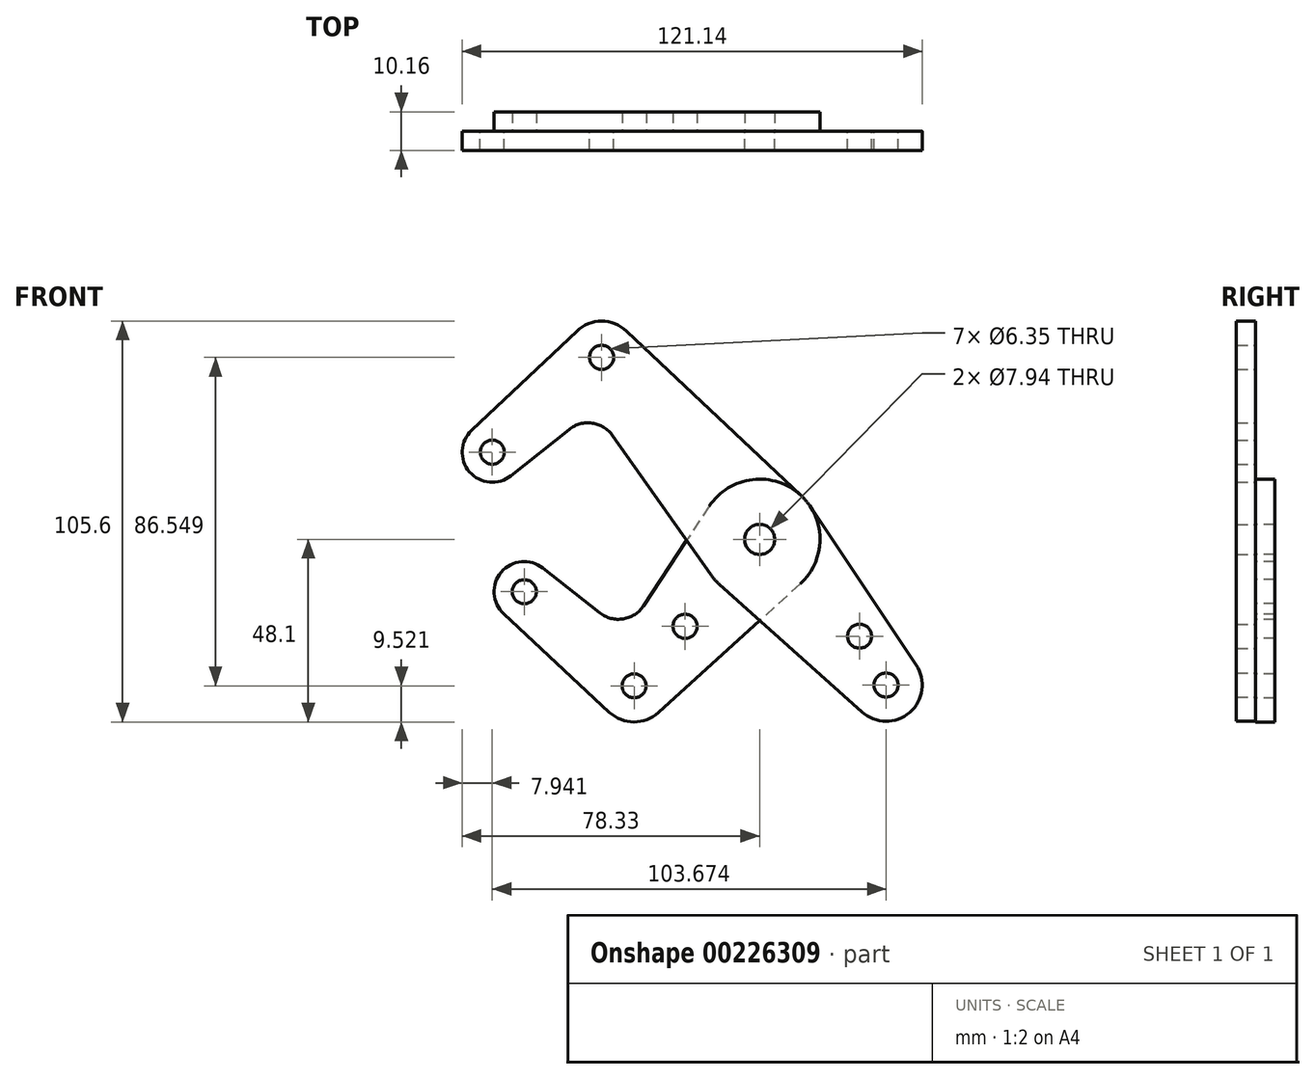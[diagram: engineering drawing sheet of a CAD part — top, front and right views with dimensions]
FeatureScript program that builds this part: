
annotation { "Feature Type Name" : "Feature", "Feature Type Description" : "" }
export const myFeature = defineFeature(function(context is Context, id is Id, definition is map)
    precondition{}
    {
        {
            var Q0;
            Q0=qCreatedBy(makeId("Front.planeOp"),FACE);
            var sketch = newSketch(context, id + "F0", { "sketchPlane" : qUnion([Q0])});
            skLineSegment(sketch, "E0", {"start": v(-41.6, 47.97) * mm, "end": v(41.6, -47.97) * mm, "construction": true});
            skCircle(sketch, "E1", {"center": v(0, 0) * mm, "radius": 3.18 * mm});
            skCircle(sketch, "E2", {"center": v(33.29, -38.38) * mm, "radius": 3.18 * mm});
            skCircle(sketch, "E3", {"center": v(-41.6, 47.97) * mm, "radius": 3.18 * mm});
            skCircle(sketch, "E4", {"center": v(-70.39, 23) * mm, "radius": 3.18 * mm});
            skLineSegment(sketch, "E5", {"start": v(-41.6, 47.97) * mm, "end": v(-70.39, 23) * mm, "construction": true});
            skCircle(sketch, "E6", {"center": v(33.29, -38.38) * mm, "radius": 9.53 * mm});
            skCircle(sketch, "E7", {"center": v(-70.39, 23) * mm, "radius": 7.94 * mm});
            skCircle(sketch, "E8", {"center": v(-41.6, 47.97) * mm, "radius": 9.53 * mm});
            skLineSegment(sketch, "E9", {"start": v(-75.83, 28.78) * mm, "end": v(-48.14, 54.9) * mm});
            skLineSegment(sketch, "E10", {"start": v(-65.44, 16.8) * mm, "end": v(-50.15, 28.98) * mm});
            skCircle(sketch, "E11", {"center": v(0, 0) * mm, "radius": 15.88 * mm});
            skLineSegment(sketch, "E12", {"start": v(-35.07, 54.9) * mm, "end": v(10.9, 11.55) * mm});
            skLineSegment(sketch, "E13", {"start": v(-38.72, 27.35) * mm, "end": v(-12.97, -9.15) * mm});
            skLineSegment(sketch, "E14", {"start": v(-10.6, -11.82) * mm, "end": v(26.93, -45.47) * mm});
            skLineSegment(sketch, "E15", {"start": v(13.2, 8.82) * mm, "end": v(41.2, -33.08) * mm});
            skArc(sketch, "E16.filletArc", {"start": v(-38.72, 27.35) * mm, "mid": v(-44.08, 30.63) * mm, "end": v(-50.15, 28.98) * mm});
            skLineSegment(sketch, "E17", {"start": v(0, 0) * mm, "end": v(-33.05, -38.58) * mm, "construction": true});
            skLineSegment(sketch, "E18", {"start": v(-33.05, -38.58) * mm, "end": v(-61.98, -13.8) * mm, "construction": true});
            skCircle(sketch, "E19", {"center": v(-61.98, -13.8) * mm, "radius": 3.18 * mm});
            skCircle(sketch, "E20", {"center": v(-33.05, -38.58) * mm, "radius": 3.18 * mm});
            skCircle(sketch, "E21", {"center": v(-61.98, -13.8) * mm, "radius": 7.94 * mm});
            skCircle(sketch, "E22", {"center": v(-33.05, -38.58) * mm, "radius": 9.53 * mm});
            skLineSegment(sketch, "E23", {"start": v(-57.08, -7.55) * mm, "end": v(-42.08, -19.35) * mm});
            skLineSegment(sketch, "E24", {"start": v(-67.4, -19.6) * mm, "end": v(-39.54, -45.55) * mm});
            skLineSegment(sketch, "E25", {"start": v(-13.25, 8.74) * mm, "end": v(-30.55, -17.48) * mm});
            skLineSegment(sketch, "E26", {"start": v(10.67, -11.75) * mm, "end": v(-26.65, -45.63) * mm});
            skArc(sketch, "E27.filletArc", {"start": v(-42.08, -19.35) * mm, "mid": v(-35.9, -20.95) * mm, "end": v(-30.55, -17.48) * mm});
            skCircle(sketch, "E28", {"center": v(-19.62, -22.9) * mm, "radius": 3.18 * mm});
            skCircle(sketch, "E29", {"center": v(26.32, -25.5) * mm, "radius": 3.18 * mm});
            skLineSegment(sketch, "E30", {"start": v(26.32, -25.5) * mm, "end": v(23.92, -27.58) * mm, "construction": true});
            skCircle(sketch, "E31", {"center": v(0, 0) * mm, "radius": 3.97 * mm});
            skSolve(sketch);
        }
        {
            var Q0;
            Q0=qCreatedBy(makeId("Front.planeOp"),FACE);
            cPlane(context, id + "F1", {"entities" : qUnion([Q0]), "cplaneType" : CPlaneType.OFFSET, "offset" : 9.52 * mm, "oppositeDirection" : true, "width" : 254 * mm, "height" : 254 * mm});
        }
        {
            var Q0;
            Q0=makeQuery(id+"F0.imprint","IMPRINT",FACE,{"disambiguationData":[TD([[makeQuery(id+"F0.imprint","IMPRINT",EDGE,{"derivedFrom":sQuery(id+"F0.wireOp",EDGE,"E4")}),-1.0]])]});
            var Q1;
            {var subQ1=sQuery(id+"F0.wireOp",EDGE,"E9");Q1=makeQuery(id+"F0.imprint","IMPRINT",FACE,{"disambiguationData":[TD([[makeQuery(id+"F0.imprint","IMPRINT",EDGE,{"derivedFrom":subQ1}),-1.0]])]});}
            var Q2;
            Q2=makeQuery(id+"F0.imprint","IMPRINT",FACE,{"disambiguationData":[TD([[makeQuery(id+"F0.imprint","IMPRINT",EDGE,{"derivedFrom":sQuery(id+"F0.wireOp",EDGE,"E3")}),-1.0]])]});
            var Q3;
            Q3=makeQuery(id+"F0.imprint","IMPRINT",FACE,{"disambiguationData":[TD([[makeQuery(id+"F0.imprint","IMPRINT",EDGE,{"derivedFrom":sQuery(id+"F0.wireOp",EDGE,"E31")}),-1.0]])]});
            var Q4;
            {var subQ0=sQuery(id+"F0.wireOp",EDGE,"E13");var subQ1=sQuery(id+"F0.wireOp",EDGE,"E11");var subQ2=makeQuery(id+"F0.imprint","INTERSECT",VERTEX,{"derivedFrom":[subQ1,subQ0]});Q4=makeQuery(id+"F0.imprint","IMPRINT",FACE,{"disambiguationData":[TD([[makeQuery(id+"F0.imprint","IMPRINT",EDGE,{"disambiguationData":[TD([[subQ2,1.0]])],"derivedFrom":subQ1}),-1.0]])]});}
            var Q5;
            {var subQ0=sQuery(id+"F0.wireOp",EDGE,"E14");var subQ1=sQuery(id+"F0.wireOp",EDGE,"E11");var subQ2=makeQuery(id+"F0.imprint","INTERSECT",VERTEX,{"derivedFrom":[subQ1,subQ0]});Q5=makeQuery(id+"F0.imprint","IMPRINT",FACE,{"disambiguationData":[TD([[makeQuery(id+"F0.imprint","IMPRINT",EDGE,{"disambiguationData":[TD([[subQ2,-1.0]])],"derivedFrom":subQ1}),-1.0]])]});}
            var Q6;
            {var subQ0=sQuery(id+"F0.wireOp",EDGE,"E15");Q6=makeQuery(id+"F0.imprint","IMPRINT",FACE,{"disambiguationData":[TD([[makeQuery(id+"F0.imprint","IMPRINT",EDGE,{"derivedFrom":subQ0}),-1.0]])]});}
            var Q7;
            Q7=makeQuery(id+"F0.imprint","IMPRINT",FACE,{"disambiguationData":[TD([[makeQuery(id+"F0.imprint","IMPRINT",EDGE,{"derivedFrom":sQuery(id+"F0.wireOp",EDGE,"E2")}),-1.0]])]});
            extrude(context, id + "F2", {"entities" : qUnion([Q0, Q1, Q2, Q3, Q4, Q5, Q6, Q7]), "depth" : 5.08 * mm});
        }
        {
            var Q0;
            {var subQ0=sQuery(id+"F0.wireOp",EDGE,"E14");var subQ1=sQuery(id+"F0.wireOp",EDGE,"E11");var subQ2=makeQuery(id+"F0.imprint","INTERSECT",VERTEX,{"derivedFrom":[subQ1,subQ0]});Q0=makeQuery(id+"F0.imprint","IMPRINT",FACE,{"disambiguationData":[TD([[makeQuery(id+"F0.imprint","IMPRINT",EDGE,{"disambiguationData":[TD([[subQ2,-1.0]])],"derivedFrom":subQ1}),-1.0]])]});}
            var Q1;
            {var subQ0=sQuery(id+"F0.wireOp",EDGE,"E13");var subQ1=sQuery(id+"F0.wireOp",EDGE,"E11");var subQ2=makeQuery(id+"F0.imprint","INTERSECT",VERTEX,{"derivedFrom":[subQ1,subQ0]});Q1=makeQuery(id+"F0.imprint","IMPRINT",FACE,{"disambiguationData":[TD([[makeQuery(id+"F0.imprint","IMPRINT",EDGE,{"disambiguationData":[TD([[subQ2,1.0]])],"derivedFrom":subQ1}),-1.0]])]});}
            var Q2;
            Q2=makeQuery(id+"F0.imprint","IMPRINT",FACE,{"disambiguationData":[TD([[makeQuery(id+"F0.imprint","IMPRINT",EDGE,{"derivedFrom":sQuery(id+"F0.wireOp",EDGE,"E31")}),-1.0]])]});
            var Q3;
            {var subQ10=sQuery(id+"F0.wireOp",EDGE,"E23");Q3=makeQuery(id+"F0.imprint","IMPRINT",FACE,{"disambiguationData":[TD([[makeQuery(id+"F0.imprint","IMPRINT",EDGE,{"derivedFrom":subQ10}),-1.0]])]});}
            var Q4;
            Q4=makeQuery(id+"F0.imprint","IMPRINT",FACE,{"disambiguationData":[TD([[makeQuery(id+"F0.imprint","IMPRINT",EDGE,{"derivedFrom":sQuery(id+"F0.wireOp",EDGE,"E20")}),-1.0]])]});
            var Q5;
            Q5=makeQuery(id+"F0.imprint","IMPRINT",FACE,{"disambiguationData":[TD([[makeQuery(id+"F0.imprint","IMPRINT",EDGE,{"derivedFrom":sQuery(id+"F0.wireOp",EDGE,"E19")}),-1.0]])]});
            extrude(context, id + "F3", {"entities" : qUnion([Q0, Q1, Q2, Q3, Q4, Q5]), "oppositeDirection" : true, "depth" : 5.08 * mm});
        }
    });
